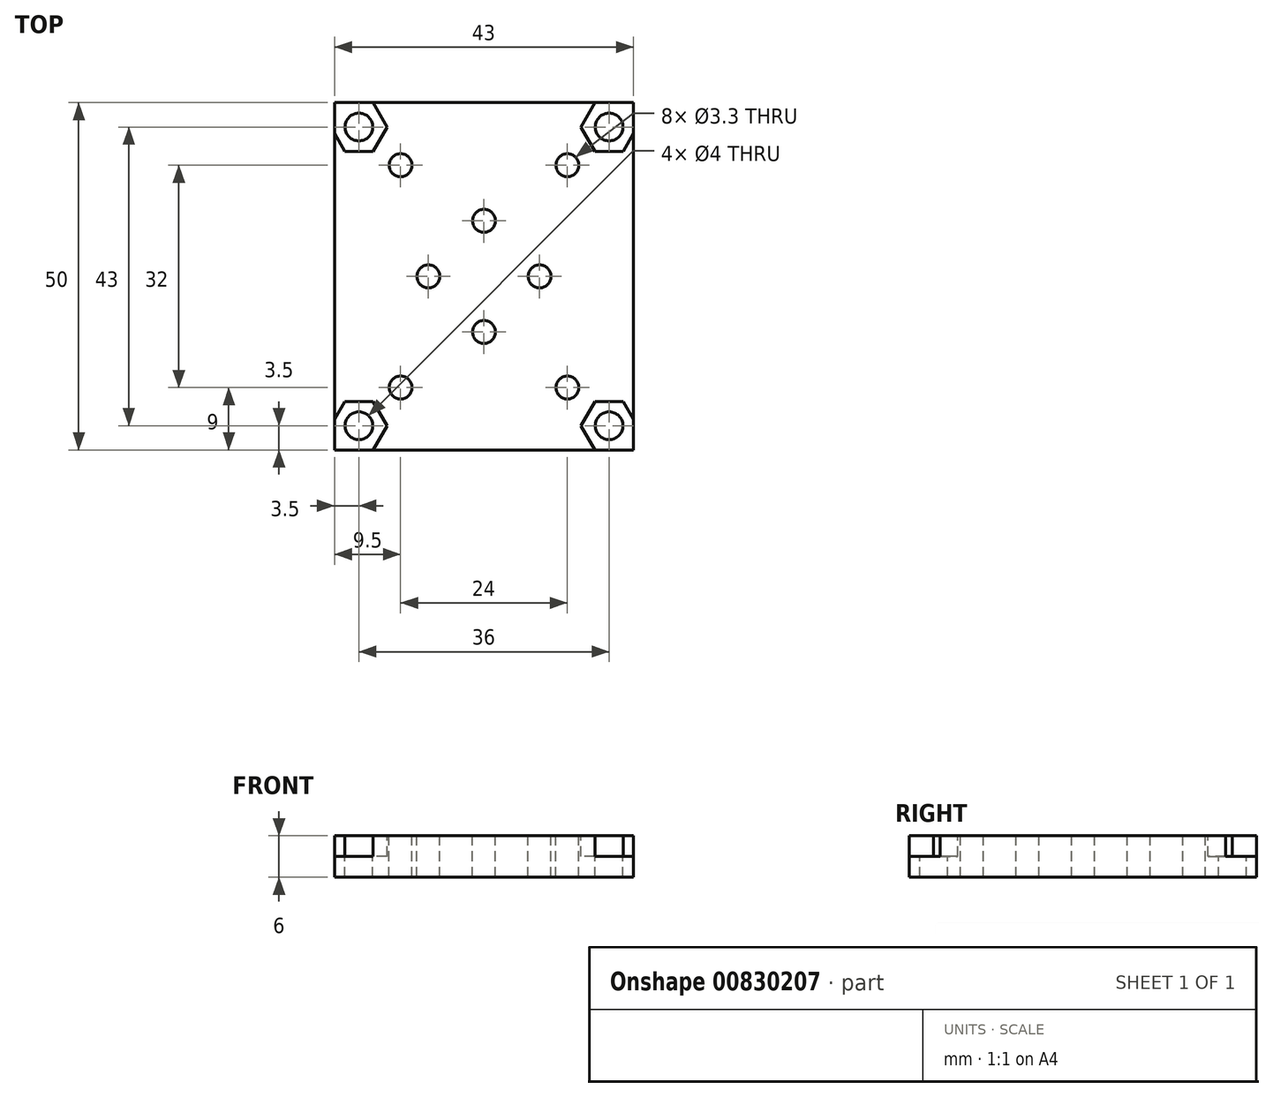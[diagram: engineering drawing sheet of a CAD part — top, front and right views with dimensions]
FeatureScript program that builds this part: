
annotation { "Feature Type Name" : "Feature", "Feature Type Description" : "" }
export const myFeature = defineFeature(function(context is Context, id is Id, definition is map)
    precondition{}
    {
        {
            var Q0;
            Q0=qCreatedBy(makeId("Top.planeOp"),FACE);
            var sketch = newSketch(context, id + "F0", { "sketchPlane" : qUnion([Q0])});
            skLineSegment(sketch, "E0", {"start": v(-21.5, 25) * mm, "end": v(21.5, 25) * mm});
            skLineSegment(sketch, "E1", {"start": v(21.5, 25) * mm, "end": v(21.5, -25) * mm});
            skLineSegment(sketch, "E2", {"start": v(21.5, -25) * mm, "end": v(-21.5, -25) * mm});
            skLineSegment(sketch, "E3", {"start": v(-21.5, -25) * mm, "end": v(-21.5, 25) * mm});
            skSolve(sketch);
        }
        {
            var Q0;
            Q0 = qSketchRegion(id + "F0", true);
            extrude(context, id + "F1", {"entities" : qUnion([Q0]), "depth" : 6 * mm, "offsetDistance" : 25 * mm});
        }
        {
            var Q0;
            Q0=makeQuery(id+"F1.opExtrude","CAP_FACE",FACE,{"disambiguationData":[OSD([sQuery(id+"F0.wireOp",EDGE,"E0"),sQuery(id+"F0.wireOp",EDGE,"E1"),sQuery(id+"F0.wireOp",EDGE,"E2"),sQuery(id+"F0.wireOp",EDGE,"E3")])],"isStart":false});
            var sketch = newSketch(context, id + "F2", { "sketchPlane" : qUnion([Q0])});
            skPoint(sketch, "E4", {"position": v(-8, 0) * mm});
            skPoint(sketch, "E5", {"position": v(8, 0) * mm});
            skPoint(sketch, "E6", {"position": v(0, -8) * mm});
            skPoint(sketch, "E7", {"position": v(0, 8) * mm});
            skPoint(sketch, "E8", {"position": v(-12, 16) * mm});
            skPoint(sketch, "E9", {"position": v(-12, -16) * mm});
            skPoint(sketch, "E10.MirrorP", {"position": v(12, 16) * mm});
            skPoint(sketch, "E11.MirrorP", {"position": v(12, -16) * mm});
            skPoint(sketch, "E12", {"position": v(-18, -21.5) * mm});
            skCircle(sketch, "E13.cCircle", {"center": v(-18, -21.5) * mm, "radius": 3.5 * mm, "construction": true});
            skLineSegment(sketch, "E13.0", {"start": v(-15.98, -25) * mm, "end": v(-20.02, -25) * mm});
            skLineSegment(sketch, "E13.1", {"start": v(-20.02, -25) * mm, "end": v(-22.04, -21.5) * mm});
            skLineSegment(sketch, "E13.2", {"start": v(-22.04, -21.5) * mm, "end": v(-20.02, -18) * mm});
            skLineSegment(sketch, "E13.3", {"start": v(-20.02, -18) * mm, "end": v(-15.98, -18) * mm});
            skLineSegment(sketch, "E13.4", {"start": v(-15.98, -18) * mm, "end": v(-13.96, -21.5) * mm});
            skLineSegment(sketch, "E13.5", {"start": v(-13.96, -21.5) * mm, "end": v(-15.98, -25) * mm});
            skPoint(sketch, "E13.0.midPoint", {"position": v(-18, -25) * mm});
            skLineSegment(sketch, "E14.MirrorCS", {"start": v(15.98, -18) * mm, "end": v(13.96, -21.5) * mm});
            skLineSegment(sketch, "E15.MirrorCS", {"start": v(15.98, -25) * mm, "end": v(20.02, -25) * mm});
            skLineSegment(sketch, "E16.MirrorCS", {"start": v(22.04, -21.5) * mm, "end": v(20.02, -18) * mm});
            skLineSegment(sketch, "E17.MirrorCS", {"start": v(20.02, -25) * mm, "end": v(22.04, -21.5) * mm});
            skLineSegment(sketch, "E18.MirrorCS", {"start": v(20.02, -18) * mm, "end": v(15.98, -18) * mm});
            skLineSegment(sketch, "E19.MirrorCS", {"start": v(13.96, -21.5) * mm, "end": v(15.98, -25) * mm});
            skPoint(sketch, "E20.MirrorP", {"position": v(18, -25) * mm});
            skPoint(sketch, "E21.MirrorP", {"position": v(18, -21.5) * mm});
            skCircle(sketch, "E22.MirrorC", {"center": v(18, -21.5) * mm, "radius": 3.5 * mm, "construction": true});
            skLineSegment(sketch, "E23.MirrorCS", {"start": v(20.02, 18) * mm, "end": v(15.98, 18) * mm});
            skLineSegment(sketch, "E24.MirrorCS", {"start": v(15.98, 25) * mm, "end": v(20.02, 25) * mm});
            skLineSegment(sketch, "E25.MirrorCS", {"start": v(22.04, 21.5) * mm, "end": v(20.02, 18) * mm});
            skPoint(sketch, "E26.MirrorP", {"position": v(18, 21.5) * mm});
            skLineSegment(sketch, "E27.MirrorCS", {"start": v(13.96, 21.5) * mm, "end": v(15.98, 25) * mm});
            skCircle(sketch, "E28.MirrorC", {"center": v(18, 21.5) * mm, "radius": 3.5 * mm, "construction": true});
            skLineSegment(sketch, "E29.MirrorCS", {"start": v(20.02, 25) * mm, "end": v(22.04, 21.5) * mm});
            skLineSegment(sketch, "E30.MirrorCS", {"start": v(15.98, 18) * mm, "end": v(13.96, 21.5) * mm});
            skPoint(sketch, "E31.MirrorP", {"position": v(18, 25) * mm});
            skLineSegment(sketch, "E32.MirrorCS", {"start": v(-13.96, 21.5) * mm, "end": v(-15.98, 25) * mm});
            skLineSegment(sketch, "E33.MirrorCS", {"start": v(-15.98, 18) * mm, "end": v(-13.96, 21.5) * mm});
            skLineSegment(sketch, "E34.MirrorCS", {"start": v(-20.02, 18) * mm, "end": v(-15.98, 18) * mm});
            skLineSegment(sketch, "E35.MirrorCS", {"start": v(-22.04, 21.5) * mm, "end": v(-20.02, 18) * mm});
            skLineSegment(sketch, "E36.MirrorCS", {"start": v(-15.98, 25) * mm, "end": v(-20.02, 25) * mm});
            skLineSegment(sketch, "E37.MirrorCS", {"start": v(-20.02, 25) * mm, "end": v(-22.04, 21.5) * mm});
            skPoint(sketch, "E38.MirrorP", {"position": v(-18, 21.5) * mm});
            skPoint(sketch, "E39.MirrorP", {"position": v(-18, 25) * mm});
            skCircle(sketch, "E40.MirrorC", {"center": v(-18, 21.5) * mm, "radius": 3.5 * mm, "construction": true});
            skSolve(sketch);
        }
        {
            var Q0;
            Q0=sQuery(id+"F2.wireOp",VERTEX,"E4");
            var Q1;
            Q1=sQuery(id+"F2.wireOp",VERTEX,"E5");
            var Q2;
            Q2=sQuery(id+"F2.wireOp",VERTEX,"E7");
            var Q3;
            Q3=sQuery(id+"F2.wireOp",VERTEX,"E6");
            var Q4;
            Q4=sQuery(id+"F2.wireOp",VERTEX,"E8");
            var Q5;
            Q5=sQuery(id+"F2.wireOp",VERTEX,"E9");
            var Q6;
            Q6=sQuery(id+"F2.wireOp",VERTEX,"E11.MirrorP");
            var Q7;
            Q7=sQuery(id+"F2.wireOp",VERTEX,"E10.MirrorP");
            var Q8;
            Q8=makeQuery(id+"F1.opExtrude","SWEPT_BODY",BODY,{"disambiguationData":[OSD([sQuery(id+"F0.wireOp",EDGE,"E0"),sQuery(id+"F0.wireOp",EDGE,"E1"),sQuery(id+"F0.wireOp",EDGE,"E2"),sQuery(id+"F0.wireOp",EDGE,"E3")])]});
            hole(context, id + "F3", {"style" : HoleStyle.SIMPLE, "endStyle" : HoleEndStyle.THROUGH, "standardTappedOrClearance" : lookupTablePath({ "standard" : "ISO", "engagement" : "75%", "pitch" : "0.7 mm", "size" : "M4", "type" : "Tapped" }), "standardBlindInLast" : lookupTablePath({ "standard" : "ISO", "engagement" : "75%", "pitch" : "0.7 mm", "size" : "M4", "type" : "Tapped" }), "holeDiameter" : 3.3 * mm, "majorDiameter" : 4 * mm, "showTappedDepth" : true, "isTappedThrough" : true, "tappedDepth" : 12 * mm, "tapClearance" : 3, "locations" : qUnion([Q0, Q1, Q2, Q3, Q4, Q5, Q6, Q7]), "scope" : qUnion([Q8])});
        }
        {
            var Q0;
            {var subQ5=sQuery(id+"F2.wireOp",EDGE,"E13.0");Q0=makeQuery(id+"F2.imprint","IMPRINT",FACE,{"disambiguationData":[TD([[makeQuery(id+"F2.imprint","IMPRINT",EDGE,{"derivedFrom":subQ5}),-1.0]])]});}
            var Q1;
            {var subQ1=makeQuery(id+"F1.opExtrude","CAP_EDGE",EDGE,{"disambiguationData":[OSD([sQuery(id+"F0.wireOp",EDGE,"E2")])],"isStart":false});var subQ3=makeQuery(id+"F1.opExtrude","CAP_EDGE",EDGE,{"disambiguationData":[OSD([sQuery(id+"F0.wireOp",EDGE,"E3")])],"isStart":false});var subQ5=makeQuery(id+"F2.imprint","INTERSECT",VERTEX,{"derivedFrom":[subQ1,subQ3]});Q1=makeQuery(id+"F2.imprint","IMPRINT",FACE,{"disambiguationData":[TD([[makeQuery(id+"F2.imprint","IMPRINT",EDGE,{"disambiguationData":[TD([[subQ5,-1.0]])],"derivedFrom":subQ3}),-1.0]])]});}
            var Q2;
            Q2=makeQuery(id+"F2.imprint","IMPRINT",FACE,{"disambiguationData":[TD([[makeQuery(id+"F2.imprint","IMPRINT",EDGE,{"derivedFrom":sQuery(id+"F2.wireOp",EDGE,"E14.MirrorCS")}),1.0]])]});
            var Q3;
            {var subQ1=makeQuery(id+"F1.opExtrude","CAP_EDGE",EDGE,{"disambiguationData":[OSD([sQuery(id+"F0.wireOp",EDGE,"E2")])],"isStart":false});var subQ3=makeQuery(id+"F1.opExtrude","CAP_EDGE",EDGE,{"disambiguationData":[OSD([sQuery(id+"F0.wireOp",EDGE,"E1")])],"isStart":false});var subQ5=makeQuery(id+"F2.imprint","INTERSECT",VERTEX,{"derivedFrom":[subQ3,subQ1]});Q3=makeQuery(id+"F2.imprint","IMPRINT",FACE,{"disambiguationData":[TD([[makeQuery(id+"F2.imprint","IMPRINT",EDGE,{"disambiguationData":[TD([[subQ5,1.0]])],"derivedFrom":subQ3}),-1.0]])]});}
            var Q4;
            {var subQ1=sQuery(id+"F2.wireOp",EDGE,"E23.MirrorCS");Q4=makeQuery(id+"F2.imprint","IMPRINT",FACE,{"disambiguationData":[TD([[makeQuery(id+"F2.imprint","IMPRINT",EDGE,{"derivedFrom":subQ1}),-1.0]])]});}
            var Q5;
            {var subQ1=makeQuery(id+"F1.opExtrude","CAP_EDGE",EDGE,{"disambiguationData":[OSD([sQuery(id+"F0.wireOp",EDGE,"E0")])],"isStart":false});var subQ3=makeQuery(id+"F1.opExtrude","CAP_EDGE",EDGE,{"disambiguationData":[OSD([sQuery(id+"F0.wireOp",EDGE,"E1")])],"isStart":false});var subQ5=makeQuery(id+"F2.imprint","INTERSECT",VERTEX,{"derivedFrom":[subQ1,subQ3]});Q5=makeQuery(id+"F2.imprint","IMPRINT",FACE,{"disambiguationData":[TD([[makeQuery(id+"F2.imprint","IMPRINT",EDGE,{"disambiguationData":[TD([[subQ5,-1.0]])],"derivedFrom":subQ3}),-1.0]])]});}
            var Q6;
            Q6=makeQuery(id+"F2.imprint","IMPRINT",FACE,{"disambiguationData":[TD([[makeQuery(id+"F2.imprint","IMPRINT",EDGE,{"derivedFrom":sQuery(id+"F2.wireOp",EDGE,"E32.MirrorCS")}),1.0]])]});
            var Q7;
            {var subQ1=makeQuery(id+"F1.opExtrude","CAP_EDGE",EDGE,{"disambiguationData":[OSD([sQuery(id+"F0.wireOp",EDGE,"E0")])],"isStart":false});var subQ3=makeQuery(id+"F1.opExtrude","CAP_EDGE",EDGE,{"disambiguationData":[OSD([sQuery(id+"F0.wireOp",EDGE,"E3")])],"isStart":false});var subQ5=makeQuery(id+"F2.imprint","INTERSECT",VERTEX,{"derivedFrom":[subQ1,subQ3]});Q7=makeQuery(id+"F2.imprint","IMPRINT",FACE,{"disambiguationData":[TD([[makeQuery(id+"F2.imprint","IMPRINT",EDGE,{"disambiguationData":[TD([[subQ5,1.0]])],"derivedFrom":subQ3}),-1.0]])]});}
            extrude(context, id + "F4", {"entities" : qUnion([Q0, Q1, Q2, Q3, Q4, Q5, Q6, Q7]), "operationType" : NewBodyOperationType.REMOVE, "oppositeDirection" : true, "depth" : 3 * mm, "offsetDistance" : 25 * mm});
        }
        {
            var Q0;
            Q0=sQuery(id+"F2.wireOp",VERTEX,"E13.cCircle.center");
            var Q1;
            Q1=sQuery(id+"F2.wireOp",VERTEX,"E22.MirrorC.center");
            var Q2;
            Q2=sQuery(id+"F2.wireOp",VERTEX,"E26.MirrorP");
            var Q3;
            Q3=sQuery(id+"F2.wireOp",VERTEX,"E38.MirrorP");
            var Q4;
            Q4=makeQuery(id+"F1.opExtrude","SWEPT_BODY",BODY,{"disambiguationData":[OSD([sQuery(id+"F0.wireOp",EDGE,"E0"),sQuery(id+"F0.wireOp",EDGE,"E1"),sQuery(id+"F0.wireOp",EDGE,"E2"),sQuery(id+"F0.wireOp",EDGE,"E3")])]});
            hole(context, id + "F5", {"style" : HoleStyle.SIMPLE, "endStyle" : HoleEndStyle.THROUGH, "holeDiameter" : 4 * mm, "majorDiameter" : 4 * mm, "isTappedThrough" : true, "tappedDepth" : 12 * mm, "tapClearance" : 3, "locations" : qUnion([Q0, Q1, Q2, Q3]), "scope" : qUnion([Q4])});
        }
    });
